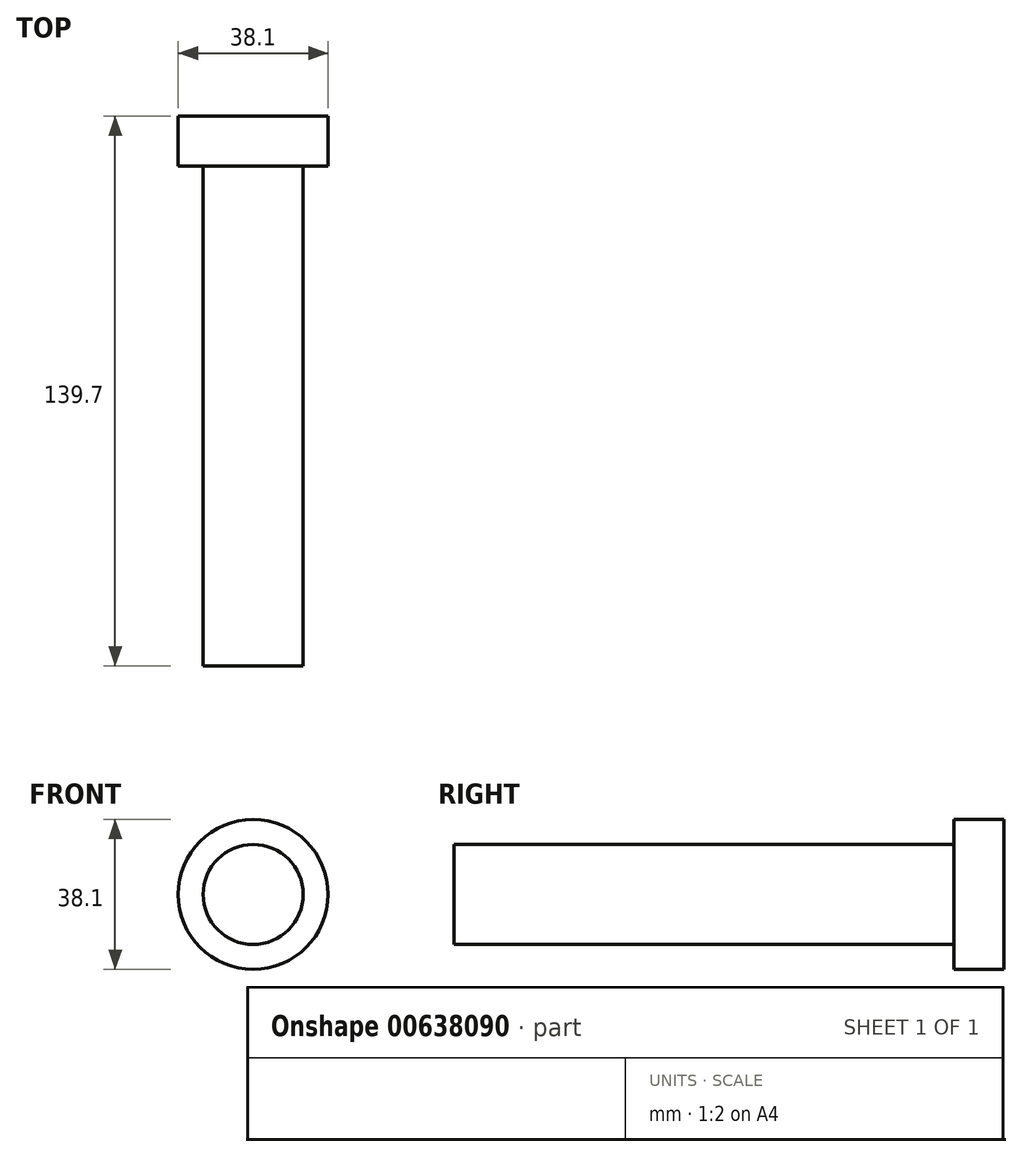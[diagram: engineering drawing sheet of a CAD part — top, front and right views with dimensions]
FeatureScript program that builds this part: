
annotation { "Feature Type Name" : "Feature", "Feature Type Description" : "" }
export const myFeature = defineFeature(function(context is Context, id is Id, definition is map)
    precondition{}
    {
        {
            var Q0;
            Q0=qCreatedBy(makeId("Front.planeOp"),FACE);
            var sketch = newSketch(context, id + "F0", { "sketchPlane" : qUnion([Q0])});
            skCircle(sketch, "E0", {"center": v(0, 0) * mm, "radius": 12.7 * mm});
            skSolve(sketch);
        }
        {
            var Q0;
            Q0=makeQuery(id+"F0.imprint","IMPRINT",FACE,{"disambiguationData":[TD([[makeQuery(id+"F0.imprint","IMPRINT",EDGE,{"derivedFrom":sQuery(id+"F0.wireOp",EDGE,"E0")}),1.0]])]});
            extrude(context, id + "F1", {"entities" : qUnion([Q0]), "depth" : 127 * mm, "offsetDistance" : 25.4 * mm});
        }
        {
            var Q0;
            Q0=makeQuery(id+"F1.opExtrude","CAP_FACE",FACE,{"disambiguationData":[OSD([sQuery(id+"F0.wireOp",EDGE,"E0")])],"isStart":true});
            var sketch = newSketch(context, id + "F2", { "sketchPlane" : qUnion([Q0])});
            skCircle(sketch, "E1", {"center": v(0, 0) * mm, "radius": 19.05 * mm});
            skSolve(sketch);
        }
        {
            var Q0;
            Q0=makeQuery(id+"F2.imprint","IMPRINT",FACE,{"disambiguationData":[TD([[makeQuery(id+"F2.imprint","IMPRINT",EDGE,{"derivedFrom":makeQuery(id+"F1.opExtrude","CAP_EDGE",EDGE,{"disambiguationData":[OSD([sQuery(id+"F0.wireOp",EDGE,"E0")])],"isStart":true})}),-1.0]])]});
            var Q1;
            Q1=makeQuery(id+"F2.imprint","IMPRINT",FACE,{"disambiguationData":[TD([[makeQuery(id+"F2.imprint","IMPRINT",EDGE,{"derivedFrom":sQuery(id+"F2.wireOp",EDGE,"E1")}),1.0]])]});
            extrude(context, id + "F3", {"entities" : qUnion([Q0, Q1]), "operationType" : NewBodyOperationType.ADD, "depth" : 12.7 * mm, "offsetDistance" : 25.4 * mm});
        }
    });
